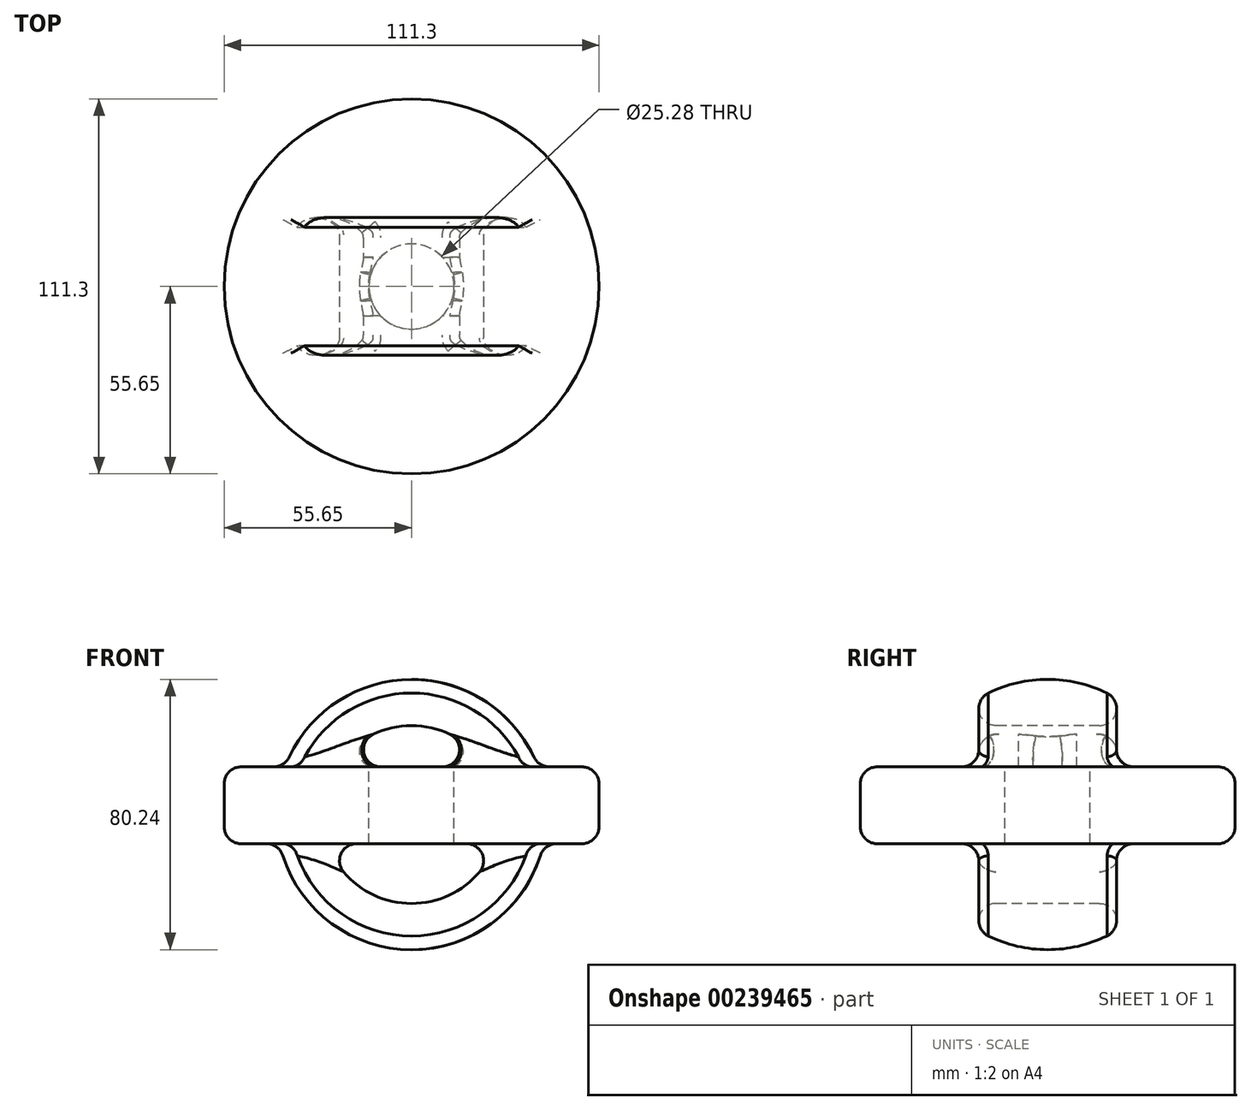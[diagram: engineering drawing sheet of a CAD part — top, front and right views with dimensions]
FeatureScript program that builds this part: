
annotation { "Feature Type Name" : "Feature", "Feature Type Description" : "" }
export const myFeature = defineFeature(function(context is Context, id is Id, definition is map)
    precondition{}
    {
        {
            var Q0;
            Q0=qCreatedBy(makeId("Front.planeOp"),FACE);
            var sketch = newSketch(context, id + "F0", { "sketchPlane" : qUnion([Q0])});
            skArc(sketch, "E0", {"start": v(0, -40.12) * mm, "mid": v(40.12, 0) * mm, "end": v(0, 40.12) * mm});
            skLineSegment(sketch, "E1", {"start": v(0, 40.12) * mm, "end": v(0, -40.12) * mm});
            skSolve(sketch);
        }
        {
            var Q0;
            Q0 = qSketchRegion(id + "F0", true);
            var Q1;
            Q1=sQuery(id+"F0.wireOp",EDGE,"E1");
            revolve(context, id + "F1", {"entities" : qUnion([Q0]), "axis" : qUnion([Q1]), "revolveType" : RevolveType.FULL});
        }
        {
            var Q0;
            Q0=qCreatedBy(makeId("Front.planeOp"),FACE);
            var sketch = newSketch(context, id + "F2", { "sketchPlane" : qUnion([Q0])});
            skCircle(sketch, "E2", {"center": v(0, 0) * mm, "radius": 26.41 * mm});
            skSolve(sketch);
        }
        {
            var Q0;
            Q0 = qSketchRegion(id + "F2", true);
            extrude(context, id + "F3", {"entities" : qUnion([Q0]), "operationType" : NewBodyOperationType.REMOVE, "endBound" : BoundingType.SYMMETRIC, "oppositeDirection" : true, "depth" : 120.4 * mm});
        }
        {
            var Q0;
            Q0=qCreatedBy(makeId("Front.planeOp"),FACE);
            var sketch = newSketch(context, id + "F4", { "sketchPlane" : qUnion([Q0])});
            skLineSegment(sketch, "E3.bottom", {"start": v(-55.65, 14.17) * mm, "end": v(-12.64, 14.17) * mm});
            skLineSegment(sketch, "E3.top", {"start": v(-55.65, -8.66) * mm, "end": v(-12.64, -8.66) * mm});
            skLineSegment(sketch, "E3.left", {"start": v(-55.65, 14.17) * mm, "end": v(-55.65, -8.66) * mm});
            skLineSegment(sketch, "E3.right", {"start": v(-12.64, 14.17) * mm, "end": v(-12.64, -8.66) * mm});
            skLineSegment(sketch, "E4", {"start": v(0, 40.06) * mm, "end": v(0, -40.06) * mm, "construction": true});
            skSolve(sketch);
        }
        {
            var Q0;
            Q0 = qSketchRegion(id + "F4", true);
            var Q1;
            Q1=sQuery(id+"F4.wireOp",EDGE,"E4");
            revolve(context, id + "F5", {"operationType" : NewBodyOperationType.ADD, "entities" : qUnion([Q0]), "axis" : qUnion([Q1]), "revolveType" : RevolveType.FULL});
        }
        {
            var Q0;
            Q0=makeQuery(id+"F5.opRevolve","SWEPT_EDGE",EDGE,{"disambiguationData":[OSD([sQuery(id+"F4.wireOp",EDGE,"E3.bottom"),sQuery(id+"F4.wireOp",EDGE,"E3.left")])]});
            var Q1;
            Q1=makeQuery(id+"F5.opRevolve","SWEPT_EDGE",EDGE,{"disambiguationData":[OSD([sQuery(id+"F4.wireOp",EDGE,"E3.top"),sQuery(id+"F4.wireOp",EDGE,"E3.left")])]});
            var Q2;
            {var subQ0=makeQuery(id+"F1.opRevolve","SWEPT_FACE",FACE,{"disambiguationData":[OSD([sQuery(id+"F0.wireOp",EDGE,"E0")])]});var subQ1=makeQuery(id+"F3.opExtrude","SWEPT_FACE",FACE,{"disambiguationData":[OSD([sQuery(id+"F2.wireOp",EDGE,"E2")])]});Q2=makeQuery(id+"F5.boolean.opBoolean","SPLIT",EDGE,{"disambiguationData":[TD([makeQuery(id+"F5.opRevolve","SWEPT_FACE",FACE,{"disambiguationData":[OSD([sQuery(id+"F4.wireOp",EDGE,"E3.top")])]})])],"derivedFrom":makeQuery(id+"F3.boolean.opBoolean","INTERSECT",EDGE,{"disambiguationData":[OD(0.0)],"derivedFrom":[subQ0,subQ1]})});}
            var Q3;
            {var subQ0=makeQuery(id+"F1.opRevolve","SWEPT_FACE",FACE,{"disambiguationData":[OSD([sQuery(id+"F0.wireOp",EDGE,"E0")])]});var subQ1=makeQuery(id+"F3.opExtrude","SWEPT_FACE",FACE,{"disambiguationData":[OSD([sQuery(id+"F2.wireOp",EDGE,"E2")])]});Q3=makeQuery(id+"F5.boolean.opBoolean","SPLIT",EDGE,{"disambiguationData":[TD([makeQuery(id+"F5.opRevolve","SWEPT_FACE",FACE,{"disambiguationData":[OSD([sQuery(id+"F4.wireOp",EDGE,"E3.top")])]})])],"derivedFrom":makeQuery(id+"F3.boolean.opBoolean","INTERSECT",EDGE,{"disambiguationData":[OD(1.0)],"derivedFrom":[subQ0,subQ1]})});}
            var Q4;
            {var subQ0=makeQuery(id+"F1.opRevolve","SWEPT_FACE",FACE,{"disambiguationData":[OSD([sQuery(id+"F0.wireOp",EDGE,"E0")])]});var subQ1=makeQuery(id+"F3.opExtrude","SWEPT_FACE",FACE,{"disambiguationData":[OSD([sQuery(id+"F2.wireOp",EDGE,"E2")])]});Q4=makeQuery(id+"F5.boolean.opBoolean","SPLIT",EDGE,{"disambiguationData":[TD([makeQuery(id+"F5.opRevolve","SWEPT_FACE",FACE,{"disambiguationData":[OSD([sQuery(id+"F4.wireOp",EDGE,"E3.bottom")])]})])],"derivedFrom":makeQuery(id+"F3.boolean.opBoolean","INTERSECT",EDGE,{"disambiguationData":[OD(1.0)],"derivedFrom":[subQ0,subQ1]})});}
            var Q5;
            {var subQ0=makeQuery(id+"F1.opRevolve","SWEPT_FACE",FACE,{"disambiguationData":[OSD([sQuery(id+"F0.wireOp",EDGE,"E0")])]});var subQ1=makeQuery(id+"F3.opExtrude","SWEPT_FACE",FACE,{"disambiguationData":[OSD([sQuery(id+"F2.wireOp",EDGE,"E2")])]});Q5=makeQuery(id+"F5.boolean.opBoolean","SPLIT",EDGE,{"disambiguationData":[TD([makeQuery(id+"F5.opRevolve","SWEPT_FACE",FACE,{"disambiguationData":[OSD([sQuery(id+"F4.wireOp",EDGE,"E3.bottom")])]})])],"derivedFrom":makeQuery(id+"F3.boolean.opBoolean","INTERSECT",EDGE,{"disambiguationData":[OD(0.0)],"derivedFrom":[subQ0,subQ1]})});}
            fillet(context, id + "F6", {"entities" : qUnion([Q0, Q1, Q2, Q3, Q4, Q5]), "radius" : 5.08 * mm, "tangentPropagation" : true, "allowEdgeOverflow" : false});
        }
        {
            var Q0;
            Q0=makeQuery(id+"F5.boolean.opBoolean","INTERSECT",EDGE,{"disambiguationData":[OD(0.0)],"derivedFrom":[makeQuery(id+"F1.opRevolve","SWEPT_FACE",FACE,{"disambiguationData":[OSD([sQuery(id+"F0.wireOp",EDGE,"E0")])]}),makeQuery(id+"F5.opRevolve","SWEPT_FACE",FACE,{"disambiguationData":[OSD([sQuery(id+"F4.wireOp",EDGE,"E3.top")])]})]});
            var Q1;
            {var subQ0=sQuery(id+"F0.wireOp",EDGE,"E0");var subQ1=makeQuery(id+"F1.opRevolve","SWEPT_FACE",FACE,{"disambiguationData":[OSD([subQ0])]});var subQ2=sQuery(id+"F2.wireOp",EDGE,"E2");var subQ3=makeQuery(id+"F3.opExtrude","SWEPT_FACE",FACE,{"disambiguationData":[OSD([subQ2])]});Q1=makeQuery(id+"F6.opFillet","BLEND_FACE",FACE,{"disambiguationData":[OSD([subQ0,subQ2]),TDD([makeQuery(id+"F5.boolean.opBoolean","SPLIT",EDGE,{"disambiguationData":[TD([makeQuery(id+"F5.opRevolve","SWEPT_FACE",FACE,{"disambiguationData":[OSD([sQuery(id+"F4.wireOp",EDGE,"E3.top")])]})])],"derivedFrom":makeQuery(id+"F3.boolean.opBoolean","INTERSECT",EDGE,{"disambiguationData":[OD(1.0)],"derivedFrom":[subQ1,subQ3]})})])]});}
            var Q2;
            Q2=makeQuery(id+"F5.boolean.opBoolean","INTERSECT",EDGE,{"disambiguationData":[OD(1.0)],"derivedFrom":[makeQuery(id+"F1.opRevolve","SWEPT_FACE",FACE,{"disambiguationData":[OSD([sQuery(id+"F0.wireOp",EDGE,"E0")])]}),makeQuery(id+"F5.opRevolve","SWEPT_FACE",FACE,{"disambiguationData":[OSD([sQuery(id+"F4.wireOp",EDGE,"E3.bottom")])]})]});
            var Q3;
            Q3=makeQuery(id+"F5.boolean.opBoolean","SPLIT",FACE,{"disambiguationData":[TD([makeQuery(id+"F5.opRevolve","SWEPT_FACE",FACE,{"disambiguationData":[OSD([sQuery(id+"F4.wireOp",EDGE,"E3.bottom")])]})])],"derivedFrom":makeQuery(id+"F1.opRevolve","SWEPT_FACE",FACE,{"disambiguationData":[OSD([sQuery(id+"F0.wireOp",EDGE,"E0")])]})});
            fillet(context, id + "F7", {"entities" : qUnion([Q0, Q1, Q2, Q3]), "radius" : 5.08 * mm, "tangentPropagation" : true, "allowEdgeOverflow" : false});
        }
    });
